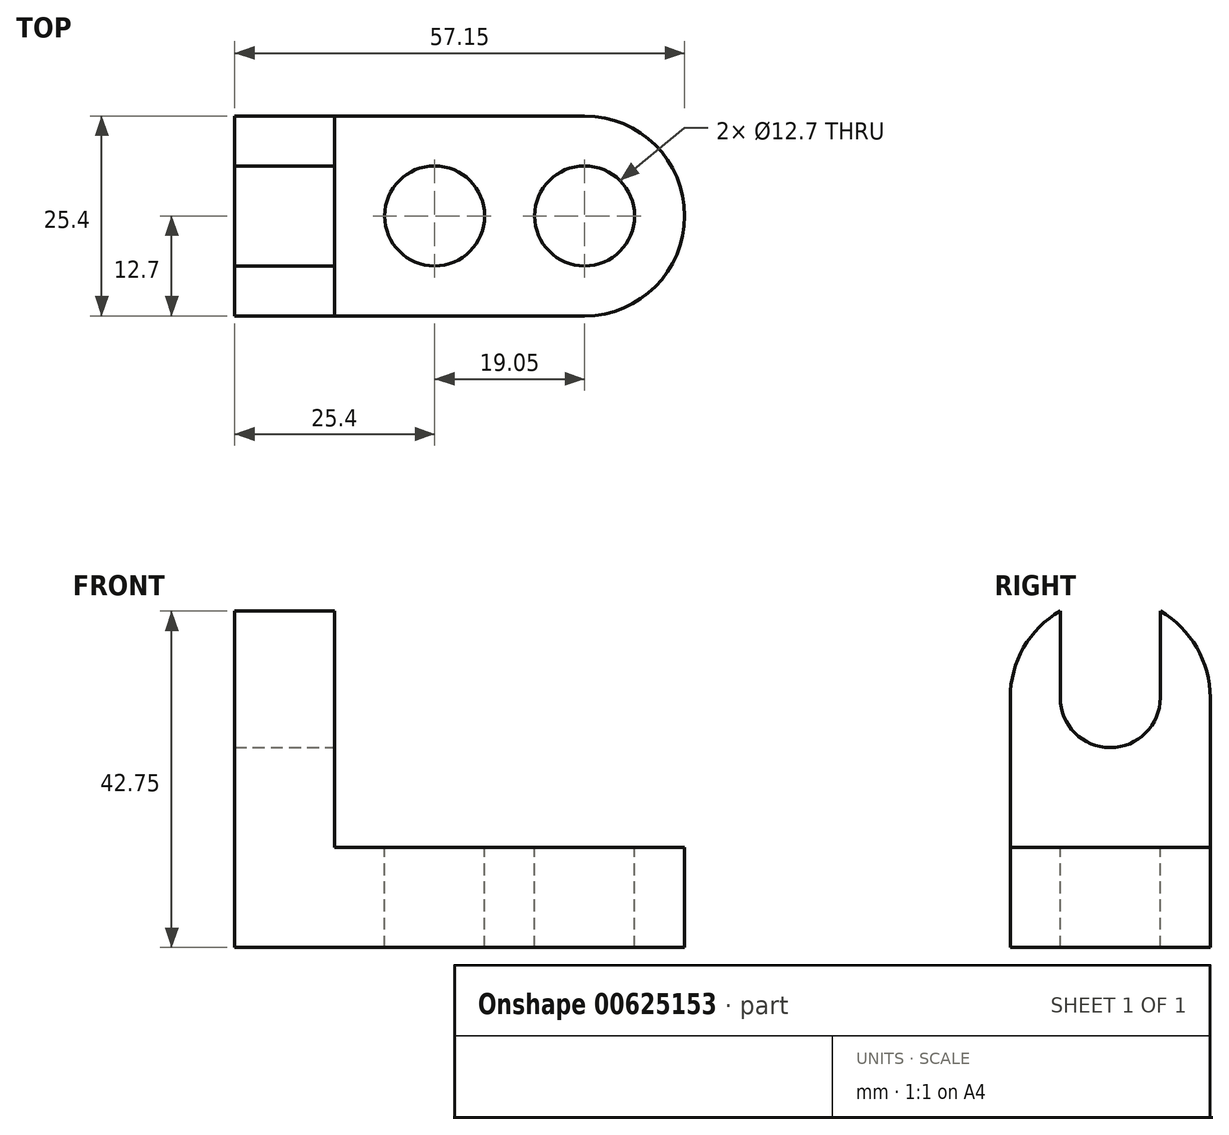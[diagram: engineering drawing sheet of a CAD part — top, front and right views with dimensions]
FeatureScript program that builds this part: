
annotation { "Feature Type Name" : "Feature", "Feature Type Description" : "" }
export const myFeature = defineFeature(function(context is Context, id is Id, definition is map)
    precondition{}
    {
        {
            var Q0;
            Q0=qCreatedBy(makeId("Front.planeOp"),FACE);
            var sketch = newSketch(context, id + "F0", { "sketchPlane" : qUnion([Q0])});
            skLineSegment(sketch, "E0.bottom", {"start": v(0, 0) * mm, "end": v(44.45, 0) * mm});
            skLineSegment(sketch, "E0.top", {"start": v(0, 31.75) * mm, "end": v(44.45, 31.75) * mm});
            skLineSegment(sketch, "E0.left", {"start": v(0, 0) * mm, "end": v(0, 31.75) * mm});
            skLineSegment(sketch, "E0.right", {"start": v(44.45, 0) * mm, "end": v(44.45, 31.75) * mm});
            skSolve(sketch);
        }
        {
            var Q0;
            Q0 = qSketchRegion(id + "F0", true);
            extrude(context, id + "F1", {"entities" : qUnion([Q0]), "depth" : 25.4 * mm, "offsetDistance" : 25.4 * mm});
        }
        {
            var Q0;
            Q0=makeQuery(id+"F1.opExtrude","CAP_FACE",FACE,{"disambiguationData":[OSD([sQuery(id+"F0.wireOp",EDGE,"E0.bottom"),sQuery(id+"F0.wireOp",EDGE,"E0.top"),sQuery(id+"F0.wireOp",EDGE,"E0.left"),sQuery(id+"F0.wireOp",EDGE,"E0.right")])],"isStart":false});
            var sketch = newSketch(context, id + "F2", { "sketchPlane" : qUnion([Q0])});
            skLineSegment(sketch, "E1", {"start": v(0, 31.75) * mm, "end": v(0, 0) * mm});
            skLineSegment(sketch, "E2", {"start": v(12.7, 31.75) * mm, "end": v(12.7, 12.7) * mm});
            skLineSegment(sketch, "E3", {"start": v(12.7, 12.7) * mm, "end": v(44.45, 12.7) * mm});
            skLineSegment(sketch, "E4", {"start": v(0, 0) * mm, "end": v(44.45, 0) * mm});
            skLineSegment(sketch, "E5", {"start": v(44.45, 12.7) * mm, "end": v(44.45, 0) * mm});
            skLineSegment(sketch, "E6", {"start": v(0, 31.75) * mm, "end": v(12.7, 31.75) * mm});
            skSolve(sketch);
        }
        {
            var Q0;
            {var subQ0=sQuery(id+"F2.wireOp",EDGE,"E2");Q0=makeQuery(id+"F2.imprint","IMPRINT",FACE,{"disambiguationData":[TD([[makeQuery(id+"F2.imprint","IMPRINT",EDGE,{"derivedFrom":subQ0}),1.0]])]});}
            extrude(context, id + "F3", {"entities" : qUnion([Q0]), "operationType" : NewBodyOperationType.REMOVE, "oppositeDirection" : true, "depth" : 25.4 * mm, "offsetDistance" : 25.4 * mm});
        }
        {
            var Q0;
            Q0=makeQuery(id+"F3.boolean.opBoolean","COPY",FACE,{"derivedFrom":makeQuery(id+"F3.opExtrude","SWEPT_FACE",FACE,{"disambiguationData":[OSD([sQuery(id+"F2.wireOp",EDGE,"E3")])]})});
            var sketch = newSketch(context, id + "F4", { "sketchPlane" : qUnion([Q0])});
            skArc(sketch, "E7", {"start": v(44.45, -25.4) * mm, "mid": v(57.15, -12.7) * mm, "end": v(44.45, 0) * mm});
            skLineSegment(sketch, "E8", {"start": v(44.45, 0) * mm, "end": v(44.45, -25.4) * mm});
            skSolve(sketch);
        }
        {
            var Q0;
            Q0=makeQuery(id+"F4.imprint","IMPRINT",FACE,{"disambiguationData":[TD([[makeQuery(id+"F4.imprint","IMPRINT",EDGE,{"derivedFrom":sQuery(id+"F4.wireOp",EDGE,"E7")}),1.0]])]});
            extrude(context, id + "F5", {"entities" : qUnion([Q0]), "operationType" : NewBodyOperationType.ADD, "oppositeDirection" : true, "depth" : 12.7 * mm, "offsetDistance" : 25.4 * mm});
        }
        {
            var Q0;
            Q0=makeQuery(id+"F3.boolean.opBoolean","COPY",FACE,{"derivedFrom":makeQuery(id+"F3.opExtrude","SWEPT_FACE",FACE,{"disambiguationData":[OSD([sQuery(id+"F2.wireOp",EDGE,"E2")])]})});
            var sketch = newSketch(context, id + "F6", { "sketchPlane" : qUnion([Q0])});
            skArc(sketch, "E9", {"start": v(0, 31.75) * mm, "mid": v(-12.7, 44.45) * mm, "end": v(-25.4, 31.75) * mm});
            skLineSegment(sketch, "E10", {"start": v(-25.4, 31.75) * mm, "end": v(0, 31.75) * mm});
            skSolve(sketch);
        }
        {
            var Q0;
            Q0=makeQuery(id+"F6.imprint","IMPRINT",FACE,{"disambiguationData":[TD([[makeQuery(id+"F6.imprint","IMPRINT",EDGE,{"derivedFrom":sQuery(id+"F6.wireOp",EDGE,"E9")}),1.0]])]});
            extrude(context, id + "F7", {"entities" : qUnion([Q0]), "operationType" : NewBodyOperationType.ADD, "oppositeDirection" : true, "depth" : 12.7 * mm, "offsetDistance" : 25.4 * mm});
        }
        {
            var Q0;
            Q0=makeQuery(id+"F7.boolean.opBoolean","MERGE",FACE,{"derivedFrom":[makeQuery(id+"F3.boolean.opBoolean","COPY",FACE,{"derivedFrom":makeQuery(id+"F3.opExtrude","SWEPT_FACE",FACE,{"disambiguationData":[OSD([sQuery(id+"F2.wireOp",EDGE,"E2")])]})}),makeQuery(id+"F7.opExtrude","CAP_FACE",FACE,{"disambiguationData":[OSD([sQuery(id+"F6.wireOp",EDGE,"E9"),sQuery(id+"F6.wireOp",EDGE,"E10")])],"isStart":true})]});
            var sketch = newSketch(context, id + "F8", { "sketchPlane" : qUnion([Q0])});
            skLineSegment(sketch, "E11", {"start": v(-19.05, 31.75) * mm, "end": v(-19.05, 42.75) * mm});
            skLineSegment(sketch, "E12", {"start": v(-6.35, 31.75) * mm, "end": v(-6.35, 42.75) * mm});
            skArc(sketch, "E13", {"start": v(-19.05, 31.75) * mm, "mid": v(-12.7, 25.4) * mm, "end": v(-6.35, 31.75) * mm});
            skSolve(sketch);
        }
        {
            var Q0;
            {var subQ0=sQuery(id+"F8.wireOp",EDGE,"E11");Q0=makeQuery(id+"F8.imprint","IMPRINT",FACE,{"disambiguationData":[TD([[makeQuery(id+"F8.imprint","IMPRINT",EDGE,{"derivedFrom":subQ0}),-1.0]])]});}
            extrude(context, id + "F9", {"entities" : qUnion([Q0]), "operationType" : NewBodyOperationType.REMOVE, "oppositeDirection" : true, "depth" : 25.4 * mm, "offsetDistance" : 25.4 * mm});
        }
        {
            var Q0;
            Q0=makeQuery(id+"F5.boolean.opBoolean","MERGE",FACE,{"derivedFrom":[makeQuery(id+"F3.boolean.opBoolean","COPY",FACE,{"derivedFrom":makeQuery(id+"F3.opExtrude","SWEPT_FACE",FACE,{"disambiguationData":[OSD([sQuery(id+"F2.wireOp",EDGE,"E3")])]})}),makeQuery(id+"F5.opExtrude","CAP_FACE",FACE,{"disambiguationData":[OSD([sQuery(id+"F4.wireOp",EDGE,"E7"),sQuery(id+"F4.wireOp",EDGE,"E8")])],"isStart":true})]});
            var sketch = newSketch(context, id + "F10", { "sketchPlane" : qUnion([Q0])});
            skCircle(sketch, "E14", {"center": v(44.45, -12.7) * mm, "radius": 6.35 * mm});
            skCircle(sketch, "E15", {"center": v(25.4, -12.7) * mm, "radius": 6.35 * mm});
            skSolve(sketch);
        }
        {
            var Q0;
            Q0=makeQuery(id+"F10.imprint","IMPRINT",FACE,{"disambiguationData":[TD([[makeQuery(id+"F10.imprint","IMPRINT",EDGE,{"derivedFrom":sQuery(id+"F10.wireOp",EDGE,"E14")}),1.0]])]});
            var Q1;
            Q1=makeQuery(id+"F10.imprint","IMPRINT",FACE,{"disambiguationData":[TD([[makeQuery(id+"F10.imprint","IMPRINT",EDGE,{"derivedFrom":sQuery(id+"F10.wireOp",EDGE,"E15")}),1.0]])]});
            extrude(context, id + "F11", {"entities" : qUnion([Q0, Q1]), "operationType" : NewBodyOperationType.REMOVE, "oppositeDirection" : true, "depth" : 25.4 * mm, "offsetDistance" : 25.4 * mm});
        }
    });
